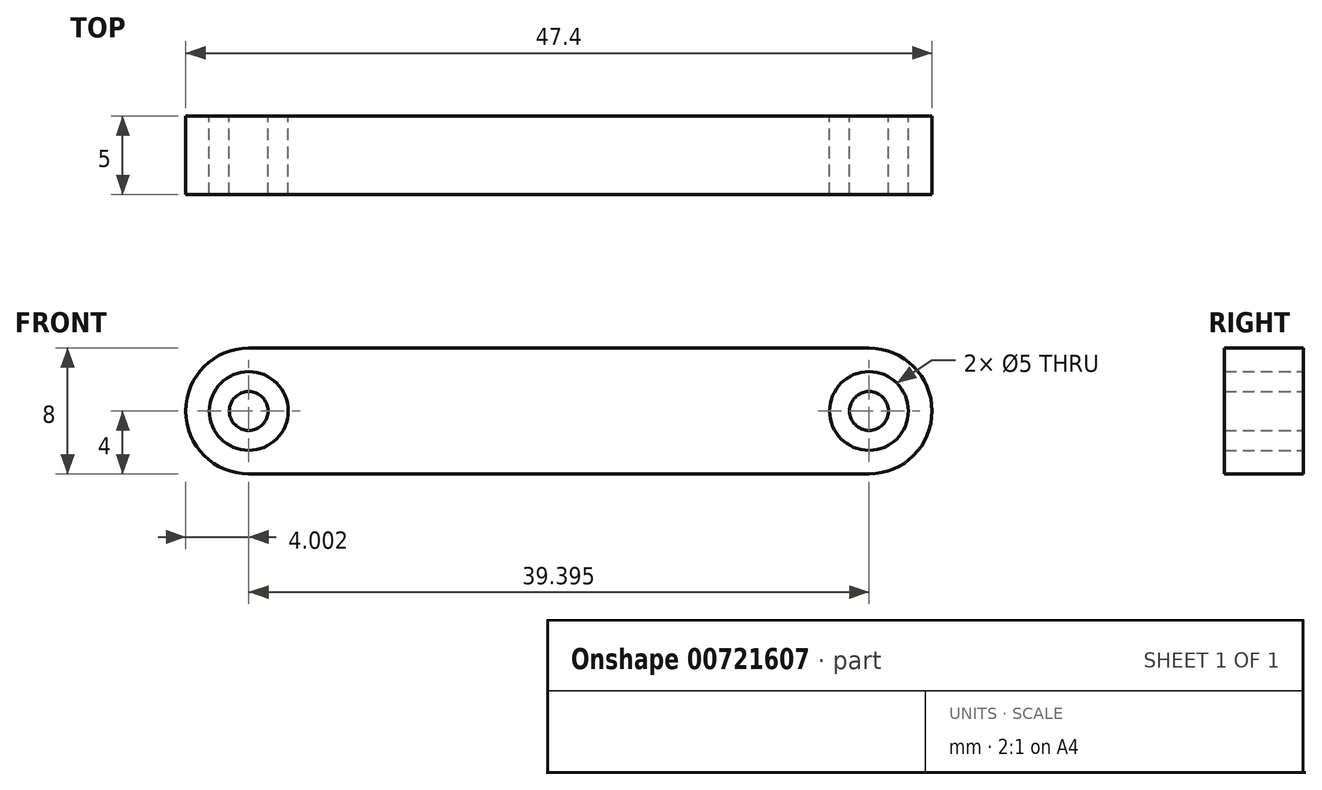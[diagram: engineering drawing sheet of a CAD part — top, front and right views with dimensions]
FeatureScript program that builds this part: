
annotation { "Feature Type Name" : "Feature", "Feature Type Description" : "" }
export const myFeature = defineFeature(function(context is Context, id is Id, definition is map)
    precondition{}
    {
        {
            var Q0;
            Q0=qCreatedBy(makeId("Front.planeOp"),FACE);
            var sketch = newSketch(context, id + "F0", { "sketchPlane" : qUnion([Q0])});
            skLineSegment(sketch, "E0.bottom", {"start": v(19.7, 4) * mm, "end": v(-19.7, 4) * mm});
            skLineSegment(sketch, "E0.top", {"start": v(19.7, -4) * mm, "end": v(-19.7, -4) * mm});
            skPoint(sketch, "E0.middle", {"position": v(0, 0) * mm});
            skArc(sketch, "E1", {"start": v(-19.7, 4) * mm, "mid": v(-23.7, 0) * mm, "end": v(-19.7, -4) * mm});
            skArc(sketch, "E2", {"start": v(19.7, -4) * mm, "mid": v(23.7, 0) * mm, "end": v(19.7, 4) * mm});
            skCircle(sketch, "E3", {"center": v(-19.7, 0) * mm, "radius": 2.5 * mm});
            skCircle(sketch, "E4", {"center": v(-19.7, 0) * mm, "radius": 1.23 * mm});
            skCircle(sketch, "E5", {"center": v(19.7, 0) * mm, "radius": 1.23 * mm});
            skCircle(sketch, "E6", {"center": v(19.7, 0) * mm, "radius": 2.5 * mm});
            skSolve(sketch);
        }
        {
            var Q0;
            Q0 = qSketchRegion(id + "F0", true);
            var Q1;
            Q1=makeQuery(id+"F0.imprint","IMPRINT",FACE,{"disambiguationData":[TD([[makeQuery(id+"F0.imprint","IMPRINT",EDGE,{"derivedFrom":sQuery(id+"F0.wireOp",EDGE,"E4")}),1.0]])]});
            var Q2;
            Q2=makeQuery(id+"F0.imprint","IMPRINT",FACE,{"disambiguationData":[TD([[makeQuery(id+"F0.imprint","IMPRINT",EDGE,{"derivedFrom":sQuery(id+"F0.wireOp",EDGE,"E5")}),1.0]])]});
            extrude(context, id + "F1", {"entities" : qUnion([Q0, Q1, Q2]), "endBound" : BoundingType.SYMMETRIC, "depth" : 5 * mm, "offsetDistance" : 25.4 * mm});
        }
    });
